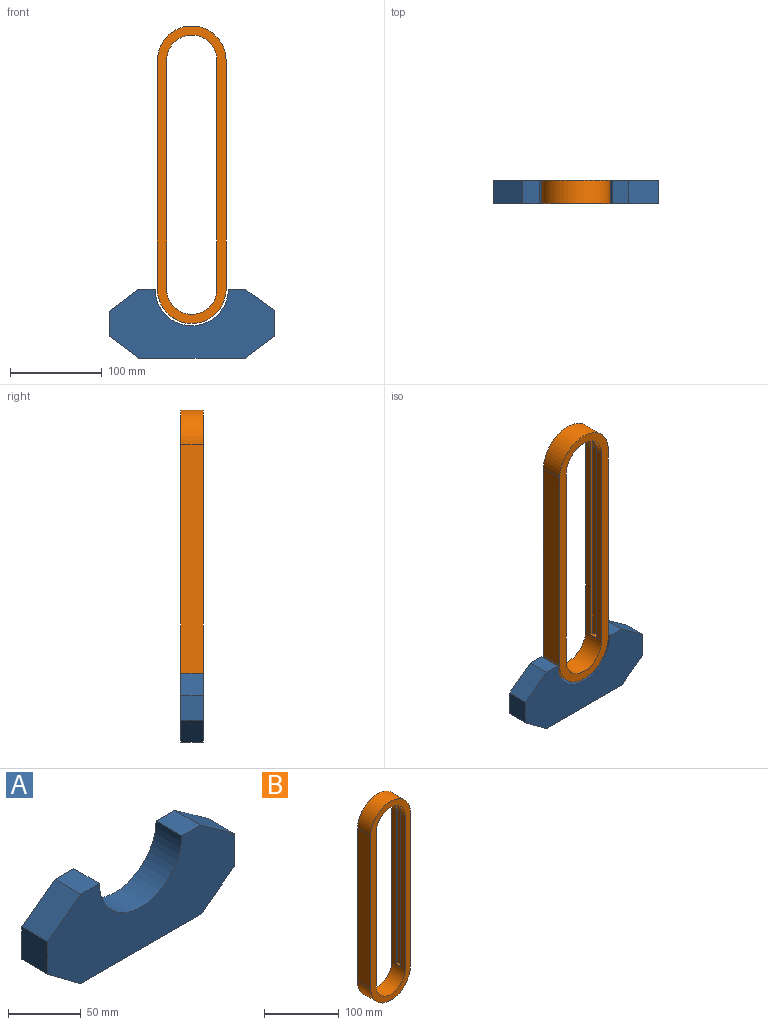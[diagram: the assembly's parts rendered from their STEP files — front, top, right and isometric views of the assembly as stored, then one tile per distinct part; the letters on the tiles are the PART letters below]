
ASSEMBLY  parts=2 mates=1
PART A: 12 faces, bbox 180.6x25x75.2 mm
  f0: plane 32x25mm, normal (-0.6,0,-0.8), area 1000mm2, adj f1,f9,f10,f11
  f1: plane 116.5x25mm, normal (0,0,-1), area 2912.5mm2, adj f0,f2,f10,f11
  f2: plane 32.05x25mm, normal (0.6,0,-0.8), area 1000mm2, adj f1,f3,f10,f11
  f3: plane 28x25mm, normal (1,0,0), area 700mm2, adj f2,f4,f10,f11
  f4: plane 32.55x25mm, normal (0.58,0,0.81), area 1000mm2, adj f3,f5,f10,f11
  f5: plane 25x18mm, normal (0,0,1), area 450mm2, adj f4,f6,f10,f11
  f6: cylinder r=40mm len=80mm, axis (0,1,0), area 3141.6mm2, adj f5,f7,f10,f11
  f7: plane 25x18mm, normal (0,0,1), area 450mm2, adj f6,f8,f10,f11
  f8: plane 32x25mm, normal (-0.6,0,0.8), area 1000mm2, adj f7,f9,f10,f11
  f9: plane 27.18x25mm, normal (-1,0,0), area 679.5mm2, adj f0,f8,f10,f11
  f10: plane 180.55x75.18mm, normal (0,-1,0), area 9530.7mm2, adj f0,f1,f2,f3,f4,f5,f6,f7
  f11: plane 180.55x75.18mm, normal (0,1,0), area 9530.7mm2, adj f0,f1,f2,f3,f4,f5,f6,f7
PART B: 22 faces, bbox 75x25x336.3 mm
  f0: cylinder r=27.5mm len=55mm, axis (0,1,0), area 2156.3mm2, adj f2,f3,f5,f6,f11,f12,f14,f15
  f1: plane 250x25mm, normal (1,0,0), area 6246.5mm2, adj f8,f13,f14,f15,f21
  f2: plane 3x3mm, normal (0,0,1), area 9mm2, adj f0,f4,f17,f21
  f3: plane 3x3mm, normal (0,0,1), area 9mm2, adj f0,f4,f19,f21
  f4: plane 250x9mm, normal (-1,0,0), area 2246.5mm2, adj f2,f3,f17,f19,f20,f21
  f5: plane 250x8mm, normal (-1,0,0), area 2000mm2, adj f0,f7,f14,f19
  f6: plane 250x8mm, normal (1,0,0), area 2000mm2, adj f0,f10,f15,f17
  f7: cylinder r=27.5mm len=55mm, axis (0,1,0), area 691.2mm2, adj f5,f12,f14,f19
  f8: cylinder r=37.5mm len=75mm, axis (0,1,0), area 2945.2mm2, adj f1,f9,f14,f15
  f9: plane 250x25mm, normal (-1,0,0), area 6250mm2, adj f8,f13,f14,f15
  f10: cylinder r=27.5mm len=55mm, axis (0,1,0), area 691.2mm2, adj f6,f11,f15,f17
  f11: plane 250x8mm, normal (-1,0,0), area 2000mm2, adj f0,f10,f15,f17
  f12: plane 250x8mm, normal (1,0,0), area 2000mm2, adj f0,f7,f14,f19
  f13: extruded ~75x37.5mm, area 2941.7mm2, adj f1,f9,f14,f15,f21
  f14: plane 336.25x75mm, normal (0,-1,0), area 7042.4mm2, adj f0,f1,f5,f7,f8,f9,f12,f13
  f15: plane 336.25x75mm, normal (0,1,0), area 7042.4mm2, adj f0,f1,f6,f8,f9,f10,f11,f13
  f16: plane 9x3mm, normal (0,0,1), area 27mm2, adj f0,f17,f18,f19
  f17: plane 280.5x61mm, normal (0,-1,0), area 1773.3mm2, adj f2,f4,f6,f10,f11,f16,f18,f20
  f18: plane 250x9mm, normal (1,0,0), area 2250mm2, adj f16,f17,f19,f20
  f19: plane 280.5x61mm, normal (0,1,0), area 1773.3mm2, adj f3,f4,f5,f7,f12,f16,f18,f20
  f20: cylinder r=30.5mm len=61mm, axis (0,1,0), area 862.4mm2, adj f4,f17,f18,f19
  f21: cylinder r=1.5mm len=10.04mm, axis (1,0,0), area 80.1mm2, adj f0,f1,f2,f3,f4,f13
PLACE A t=(-0.46,7.88,-21.78)mm
PLACE B t=(-37.96,7.88,26.45)mm
MATE revolute A.f6 <-> B.f0  axis (0,-1,0) through (-0.46,-17.12,26.45)mm
